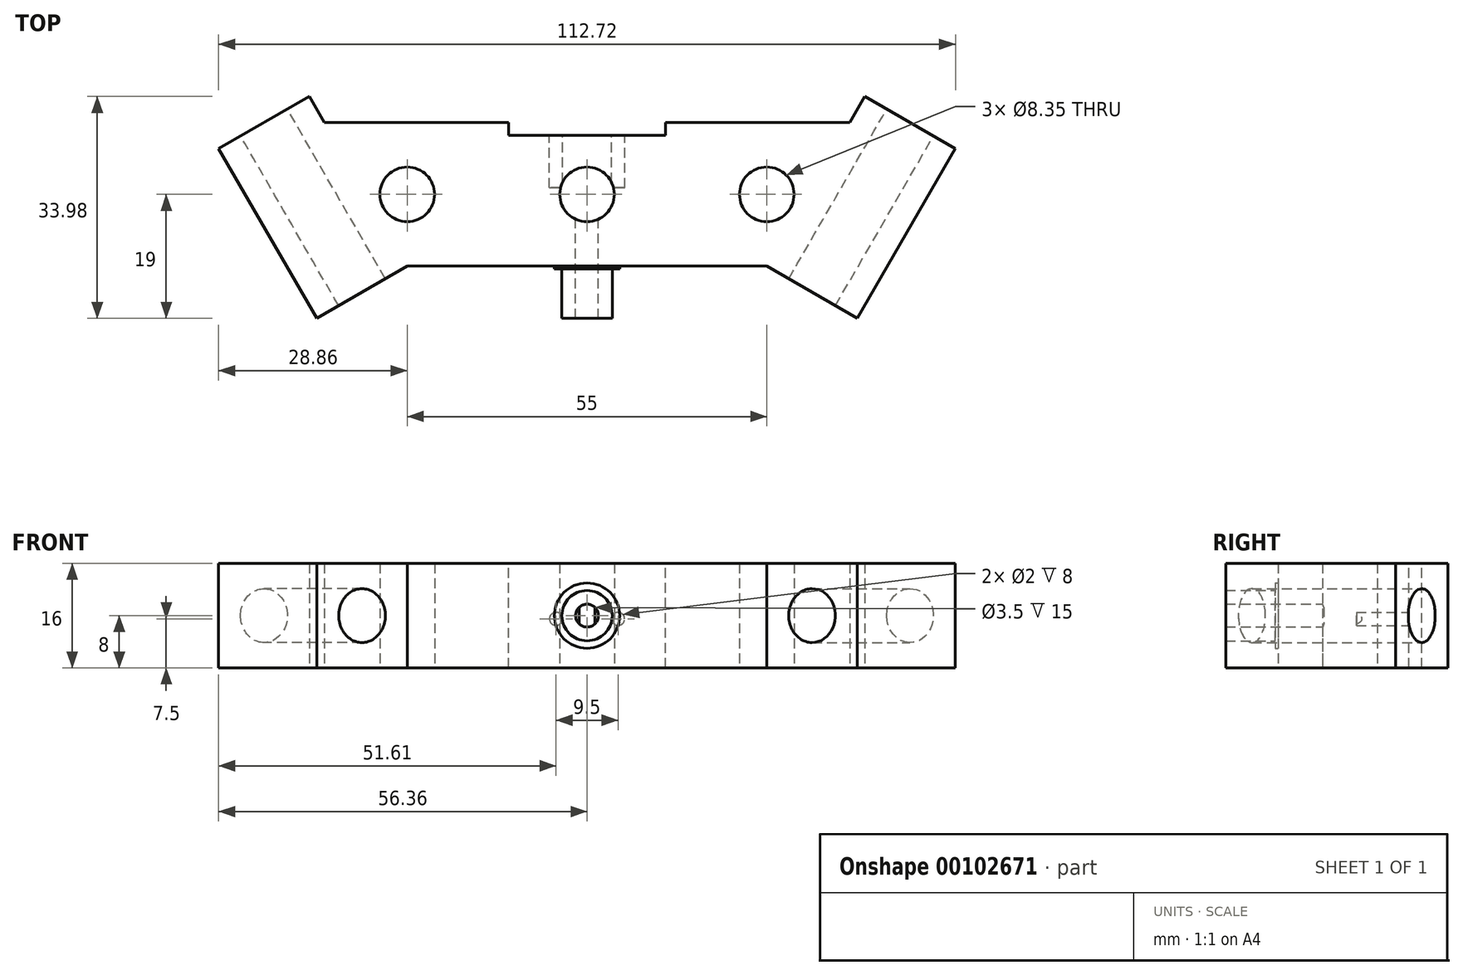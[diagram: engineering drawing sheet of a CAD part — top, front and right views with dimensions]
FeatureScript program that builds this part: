
annotation { "Feature Type Name" : "Feature", "Feature Type Description" : "" }
export const myFeature = defineFeature(function(context is Context, id is Id, definition is map)
    precondition{}
    {
        {
            var Q0;
            Q0=qCreatedBy(makeId("Top.planeOp"),FACE);
            var sketch = newSketch(context, id + "F0", { "sketchPlane" : qUnion([Q0])});
            skCircle(sketch, "E0", {"center": v(-27.5, 0) * mm, "radius": 4.17 * mm});
            skLineSegment(sketch, "E1", {"start": v(-56.36, 6.98) * mm, "end": v(-42.5, 14.98) * mm});
            skLineSegment(sketch, "E2", {"start": v(-42.5, 14.98) * mm, "end": v(-40.2, 11) * mm});
            skLineSegment(sketch, "E3", {"start": v(-27.5, -11) * mm, "end": v(-41.36, -19) * mm});
            skLineSegment(sketch, "E4", {"start": v(-41.36, -19) * mm, "end": v(-56.36, 6.98) * mm});
            skLineSegment(sketch, "E5", {"start": v(-27.5, 0) * mm, "end": v(-27.5, -11) * mm, "construction": true});
            skLineSegment(sketch, "E6.MirrorCS", {"start": v(42.5, 14.98) * mm, "end": v(40.2, 11) * mm});
            skLineSegment(sketch, "E7.MirrorCS", {"start": v(41.36, -19) * mm, "end": v(56.36, 6.98) * mm});
            skLineSegment(sketch, "E8.MirrorCS", {"start": v(27.5, -11) * mm, "end": v(41.36, -19) * mm});
            skLineSegment(sketch, "E9.MirrorCS", {"start": v(56.36, 6.98) * mm, "end": v(42.5, 14.98) * mm});
            skLineSegment(sketch, "E10.MirrorCS", {"start": v(27.5, 0) * mm, "end": v(27.5, -11) * mm, "construction": true});
            skCircle(sketch, "E11.MirrorC", {"center": v(27.5, 0) * mm, "radius": 4.17 * mm});
            skLineSegment(sketch, "E12", {"start": v(-40.2, 11) * mm, "end": v(0, 11) * mm});
            skLineSegment(sketch, "E13", {"start": v(0, 11) * mm, "end": v(40.2, 11) * mm});
            skLineSegment(sketch, "E14", {"start": v(-27.5, -11) * mm, "end": v(27.5, -11) * mm});
            skLineSegment(sketch, "E15", {"start": v(0, 0) * mm, "end": v(27.5, 0) * mm, "construction": true});
            skLineSegment(sketch, "E16", {"start": v(0, 0) * mm, "end": v(-27.5, 0) * mm, "construction": true});
            skCircle(sketch, "E17", {"center": v(0, 0) * mm, "radius": 4.17 * mm});
            skSolve(sketch);
        }
        {
            var Q0;
            Q0=makeQuery(id+"F0.imprint","IMPRINT",FACE,{"disambiguationData":[TD([[makeQuery(id+"F0.imprint","IMPRINT",EDGE,{"derivedFrom":sQuery(id+"F0.wireOp",EDGE,"E0")}),-1.0]])]});
            extrude(context, id + "F1", {"entities" : qUnion([Q0]), "depth" : 16 * mm});
        }
        {
            var Q0;
            Q0=makeQuery(id+"F1.opExtrude","SWEPT_FACE",FACE,{"disambiguationData":[OSD([sQuery(id+"F0.wireOp",EDGE,"E9.MirrorCS")])]});
            var sketch = newSketch(context, id + "F2", { "sketchPlane" : qUnion([Q0])});
            skCircle(sketch, "E18", {"center": v(-37.32, 8) * mm, "radius": 4.12 * mm});
            skPoint(sketch, "E18.centerSnap0", {"position": v(-29.32, 8) * mm});
            skPoint(sketch, "E18.centerSnap1", {"position": v(-37.32, 16) * mm});
            skSolve(sketch);
        }
        {
            var Q0;
            Q0=makeQuery(id+"F2.imprint","IMPRINT",FACE,{"disambiguationData":[TD([[makeQuery(id+"F2.imprint","IMPRINT",EDGE,{"derivedFrom":sQuery(id+"F2.wireOp",EDGE,"E18")}),1.0]])]});
            extrude(context, id + "F3", {"entities" : qUnion([Q0]), "operationType" : NewBodyOperationType.REMOVE, "oppositeDirection" : true, "depth" : 40 * mm});
        }
        {
            var Q0;
            Q0=makeQuery(id+"F1.opExtrude","SWEPT_FACE",FACE,{"disambiguationData":[OSD([sQuery(id+"F0.wireOp",EDGE,"E1")])]});
            var sketch = newSketch(context, id + "F4", { "sketchPlane" : qUnion([Q0])});
            skCircle(sketch, "E19", {"center": v(37.32, 8) * mm, "radius": 4.12 * mm});
            skPoint(sketch, "E19.centerSnap0", {"position": v(29.32, 8) * mm});
            skPoint(sketch, "E19.centerSnap1", {"position": v(37.32, 16) * mm});
            skSolve(sketch);
        }
        {
            var Q0;
            Q0 = qSketchRegion(id + "F4", true);
            extrude(context, id + "F5", {"entities" : qUnion([Q0]), "operationType" : NewBodyOperationType.REMOVE, "oppositeDirection" : true, "depth" : 40 * mm});
        }
        {
            var Q0;
            Q0=makeQuery(id+"F1.opExtrude","SWEPT_FACE",FACE,{"disambiguationData":[OSD([sQuery(id+"F0.wireOp",EDGE,"E14")])]});
            var sketch = newSketch(context, id + "F6", { "sketchPlane" : qUnion([Q0])});
            skCircle(sketch, "E20", {"center": v(0, 8) * mm, "radius": 3.85 * mm});
            skPoint(sketch, "E20.centerSnap0", {"position": v(-27.5, 8) * mm});
            skPoint(sketch, "E20.centerSnap1", {"position": v(0, 0) * mm});
            skCircle(sketch, "E21", {"center": v(0, 8) * mm, "radius": 1.75 * mm});
            skCircle(sketch, "E22", {"center": v(0, 8) * mm, "radius": 5 * mm});
            skSolve(sketch);
        }
        {
            var Q0;
            Q0=makeQuery(id+"F6.imprint","IMPRINT",FACE,{"disambiguationData":[TD([[makeQuery(id+"F6.imprint","IMPRINT",EDGE,{"derivedFrom":sQuery(id+"F6.wireOp",EDGE,"E20")}),1.0]])]});
            extrude(context, id + "F7", {"entities" : qUnion([Q0]), "operationType" : NewBodyOperationType.ADD, "depth" : 8 * mm});
        }
        {
            var Q0;
            Q0=makeQuery(id+"F7.boolean.opBoolean","SPLIT",FACE,{"disambiguationData":[TD([makeQuery(id+"F7.opExtrude","SWEPT_FACE",FACE,{"disambiguationData":[OSD([sQuery(id+"F6.wireOp",EDGE,"E21")])]})])],"derivedFrom":makeQuery(id+"F1.opExtrude","SWEPT_FACE",FACE,{"disambiguationData":[OSD([sQuery(id+"F0.wireOp",EDGE,"E14")])]})});
            extrude(context, id + "F8", {"entities" : qUnion([Q0]), "operationType" : NewBodyOperationType.REMOVE, "oppositeDirection" : true, "depth" : 7 * mm});
        }
        {
            var Q0;
            Q0=makeQuery(id+"F6.imprint","IMPRINT",FACE,{"disambiguationData":[TD([[makeQuery(id+"F6.imprint","IMPRINT",EDGE,{"derivedFrom":sQuery(id+"F6.wireOp",EDGE,"E20")}),-1.0]])]});
            extrude(context, id + "F9", {"entities" : qUnion([Q0]), "operationType" : NewBodyOperationType.ADD, "depth" : .4 * mm});
        }
        {
            var Q0;
            Q0=makeQuery(id+"F1.opExtrude","SWEPT_FACE",FACE,{"disambiguationData":[OSD([sQuery(id+"F0.wireOp",EDGE,"E12"),sQuery(id+"F0.wireOp",EDGE,"E13")])]});
            var sketch = newSketch(context, id + "F10", { "sketchPlane" : qUnion([Q0])});
            skLineSegment(sketch, "E23", {"start": v(0, 0) * mm, "end": v(0, 7.5) * mm, "construction": true});
            skPoint(sketch, "E23.endSnap0", {"position": v(0, 0) * mm});
            skLineSegment(sketch, "E24", {"start": v(0, 7.5) * mm, "end": v(-4.75, 7.5) * mm, "construction": true});
            skLineSegment(sketch, "E25", {"start": v(0, 7.5) * mm, "end": v(4.75, 7.5) * mm, "construction": true});
            skCircle(sketch, "E26", {"center": v(-4.75, 7.5) * mm, "radius": 1 * mm});
            skCircle(sketch, "E27", {"center": v(4.75, 7.5) * mm, "radius": 1 * mm});
            skSolve(sketch);
        }
        {
            var Q0;
            Q0=makeQuery(id+"F10.imprint","IMPRINT",FACE,{"disambiguationData":[TD([[makeQuery(id+"F10.imprint","IMPRINT",EDGE,{"derivedFrom":sQuery(id+"F10.wireOp",EDGE,"E26")}),1.0]])]});
            var Q1;
            Q1=makeQuery(id+"F10.imprint","IMPRINT",FACE,{"disambiguationData":[TD([[makeQuery(id+"F10.imprint","IMPRINT",EDGE,{"derivedFrom":sQuery(id+"F10.wireOp",EDGE,"E27")}),1.0]])]});
            extrude(context, id + "F11", {"entities" : qUnion([Q0, Q1]), "operationType" : NewBodyOperationType.REMOVE, "oppositeDirection" : true, "depth" : 10 * mm});
        }
        {
            var Q0;
            Q0=makeQuery(id+"F1.opExtrude","SWEPT_FACE",FACE,{"disambiguationData":[OSD([sQuery(id+"F0.wireOp",EDGE,"E12"),sQuery(id+"F0.wireOp",EDGE,"E13")])]});
            var sketch = newSketch(context, id + "F12", { "sketchPlane" : qUnion([Q0])});
            skLineSegment(sketch, "E28.bottom", {"start": v(12, 0) * mm, "end": v(-12, 0) * mm});
            skLineSegment(sketch, "E28.top", {"start": v(12, 16) * mm, "end": v(-12, 16) * mm});
            skLineSegment(sketch, "E28.left", {"start": v(12, 0) * mm, "end": v(12, 16) * mm});
            skLineSegment(sketch, "E28.right", {"start": v(-12, 0) * mm, "end": v(-12, 16) * mm});
            skSolve(sketch);
        }
        {
            var Q0;
            Q0=makeQuery(id+"F12.imprint","IMPRINT",FACE,{"disambiguationData":[TD([[makeQuery(id+"F12.imprint","IMPRINT",EDGE,{"derivedFrom":sQuery(id+"F12.wireOp",EDGE,"E28.bottom")}),-1.0]])]});
            extrude(context, id + "F13", {"entities" : qUnion([Q0]), "operationType" : NewBodyOperationType.REMOVE, "oppositeDirection" : true, "depth" : 2 * mm});
        }
    });
